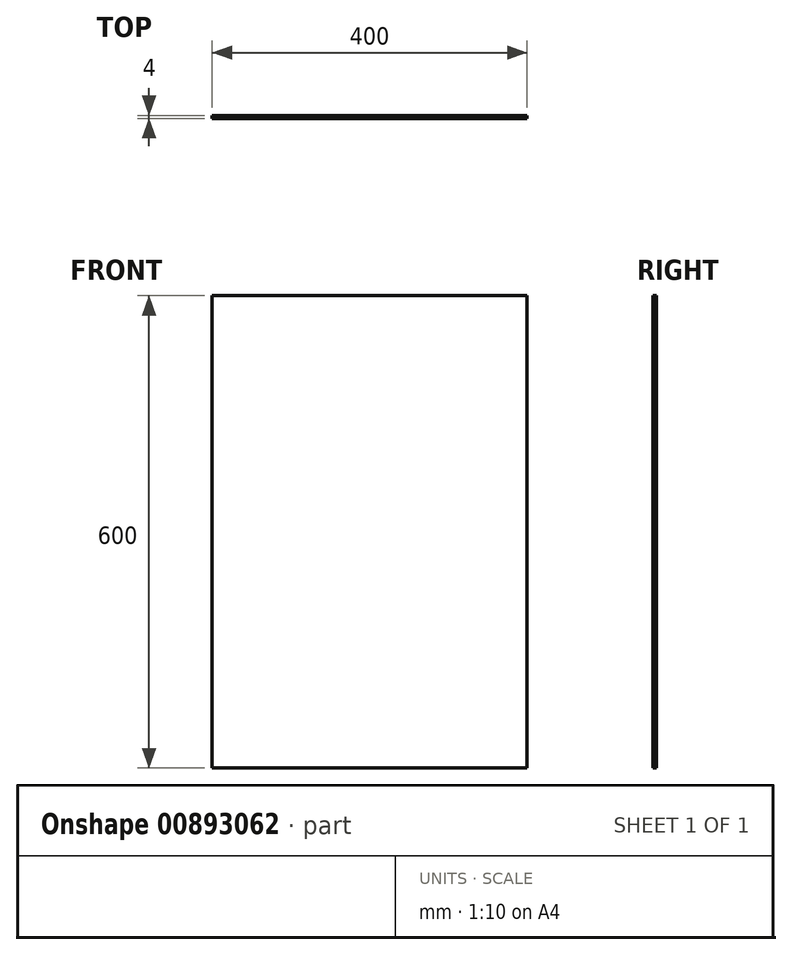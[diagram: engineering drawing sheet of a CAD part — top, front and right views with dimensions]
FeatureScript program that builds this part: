
annotation { "Feature Type Name" : "Feature", "Feature Type Description" : "" }
export const myFeature = defineFeature(function(context is Context, id is Id, definition is map)
    precondition{}
    {
        {
            var Q0;
            Q0=qCreatedBy(makeId("Front.planeOp"),FACE);
            var sketch = newSketch(context, id + "F0", { "sketchPlane" : qUnion([Q0])});
            skLineSegment(sketch, "E0.bottom", {"start": v(200, 300) * mm, "end": v(-200, 300) * mm});
            skLineSegment(sketch, "E0.top", {"start": v(200, -300) * mm, "end": v(-200, -300) * mm});
            skLineSegment(sketch, "E0.left", {"start": v(200, 300) * mm, "end": v(200, -300) * mm});
            skLineSegment(sketch, "E0.right", {"start": v(-200, 300) * mm, "end": v(-200, -300) * mm});
            skPoint(sketch, "E0.middle", {"position": v(0, 0) * mm});
            skSolve(sketch);
        }
        {
            var Q0;
            Q0=makeQuery(id+"F0.imprint","IMPRINT",FACE,{"disambiguationData":[TD([[makeQuery(id+"F0.imprint","IMPRINT",EDGE,{"derivedFrom":sQuery(id+"F0.wireOp",EDGE,"E0.bottom")}),1.0]])]});
            extrude(context, id + "F1", {"entities" : qUnion([Q0]), "depth" : 4 * mm, "offsetDistance" : 25 * mm});
        }
    });
